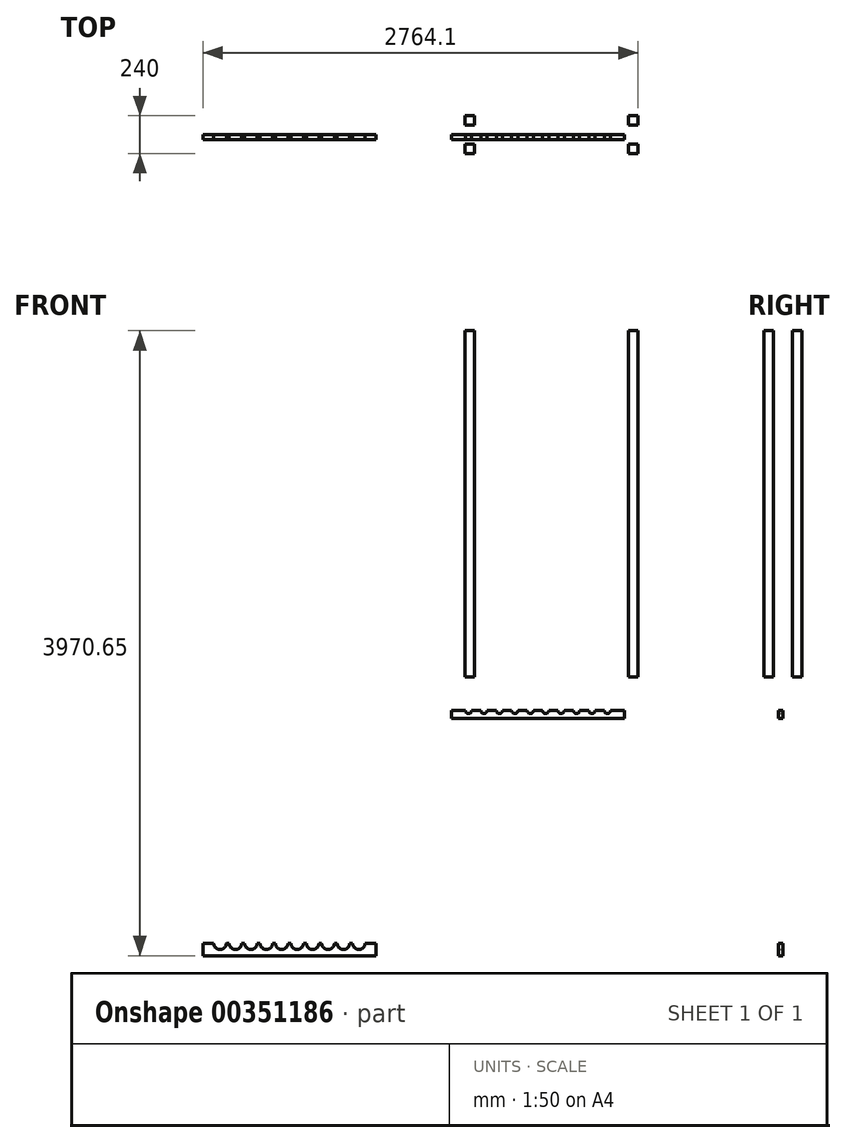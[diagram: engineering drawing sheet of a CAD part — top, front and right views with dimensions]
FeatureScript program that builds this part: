
annotation { "Feature Type Name" : "Feature", "Feature Type Description" : "" }
export const myFeature = defineFeature(function(context is Context, id is Id, definition is map)
    precondition{}
    {
        {
            var Q0;
            Q0=qCreatedBy(makeId("Top.planeOp"),FACE);
            var sketch = newSketch(context, id + "F0", { "sketchPlane" : qUnion([Q0])});
            skLineSegment(sketch, "E0.bottom", {"start": v(-550, -60) * mm, "end": v(-490, -60) * mm});
            skLineSegment(sketch, "E0.top", {"start": v(-550, -120) * mm, "end": v(-490, -120) * mm});
            skLineSegment(sketch, "E0.left", {"start": v(-550, -60) * mm, "end": v(-550, -120) * mm});
            skLineSegment(sketch, "E0.right", {"start": v(-490, -60) * mm, "end": v(-490, -120) * mm});
            skLineSegment(sketch, "E1.bottom", {"start": v(490, -60) * mm, "end": v(550, -60) * mm});
            skLineSegment(sketch, "E1.top", {"start": v(490, -120) * mm, "end": v(550, -120) * mm});
            skLineSegment(sketch, "E1.left", {"start": v(490, -60) * mm, "end": v(490, -120) * mm});
            skLineSegment(sketch, "E1.right", {"start": v(550, -60) * mm, "end": v(550, -120) * mm});
            skLineSegment(sketch, "E2", {"start": v(0, 0) * mm, "end": v(566.52, 0) * mm});
            skLineSegment(sketch, "E3.MirrorCS", {"start": v(550, 60) * mm, "end": v(550, 120) * mm});
            skLineSegment(sketch, "E4.MirrorCS", {"start": v(-550, 60) * mm, "end": v(-550, 120) * mm});
            skLineSegment(sketch, "E5.MirrorCS", {"start": v(-490, 60) * mm, "end": v(-490, 120) * mm});
            skLineSegment(sketch, "E6.MirrorCS", {"start": v(490, 60) * mm, "end": v(490, 120) * mm});
            skLineSegment(sketch, "E7.MirrorCS", {"start": v(490, 60) * mm, "end": v(550, 60) * mm});
            skLineSegment(sketch, "E8.MirrorCS", {"start": v(-550, 120) * mm, "end": v(-490, 120) * mm});
            skLineSegment(sketch, "E9.MirrorCS", {"start": v(-550, 60) * mm, "end": v(-490, 60) * mm});
            skLineSegment(sketch, "E10.MirrorCS", {"start": v(490, 120) * mm, "end": v(550, 120) * mm});
            skSolve(sketch);
        }
        {
            var Q0;
            Q0 = qSketchRegion(id + "F0", true);
            var Q1;
            Q1 = qSketchRegion(id + "FOOtY1L82Ux6p5i_4", true);
            extrude(context, id + "F1", {"entities" : qUnion([Q0, Q1]), "depth" : 2200 * mm});
        }
        {
            var Q0;
            Q0=qCreatedBy(makeId("Front.planeOp"),FACE);
            var sketch = newSketch(context, id + "F2", { "sketchPlane" : qUnion([Q0])});
            skLineSegment(sketch, "E11.bottom", {"start": v(-635.8, -212.51) * mm, "end": v(464.2, -212.51) * mm});
            skLineSegment(sketch, "E11.top", {"start": v(-635.8, -262.51) * mm, "end": v(464.2, -262.51) * mm});
            skLineSegment(sketch, "E11.left", {"start": v(-635.8, -212.51) * mm, "end": v(-635.8, -262.51) * mm});
            skLineSegment(sketch, "E11.right", {"start": v(464.2, -212.51) * mm, "end": v(464.2, -262.51) * mm});
            skCircle(sketch, "E12", {"center": v(-526.8, -212.51) * mm, "radius": 20 * mm});
            skCircle(sketch, "E13.1.0.0", {"center": v(-428.8, -212.51) * mm, "radius": 20 * mm});
            skCircle(sketch, "E13.2.0.0", {"center": v(-330.8, -212.51) * mm, "radius": 20 * mm});
            skCircle(sketch, "E13.3.0.0", {"center": v(-232.8, -212.51) * mm, "radius": 20 * mm});
            skCircle(sketch, "E13.4.0.0", {"center": v(-134.8, -212.51) * mm, "radius": 20 * mm});
            skCircle(sketch, "E13.5.0.0", {"center": v(-36.8, -212.51) * mm, "radius": 20 * mm});
            skCircle(sketch, "E13.6.0.0", {"center": v(61.2, -212.51) * mm, "radius": 20 * mm});
            skCircle(sketch, "E13.7.0.0", {"center": v(159.2, -212.51) * mm, "radius": 20 * mm});
            skCircle(sketch, "E13.8.0.0", {"center": v(257.2, -212.51) * mm, "radius": 20 * mm});
            skCircle(sketch, "E13.9.0.0", {"center": v(355.2, -212.51) * mm, "radius": 20 * mm});
            skLineSegment(sketch, "E13.direction1", {"start": v(-526.8, -212.51) * mm, "end": v(-428.8, -212.51) * mm, "construction": true});
            skLineSegment(sketch, "E14.bottom", {"start": v(-2214.1, -1690.65) * mm, "end": v(-1114.1, -1690.65) * mm});
            skLineSegment(sketch, "E14.top", {"start": v(-2214.1, -1770.65) * mm, "end": v(-1114.1, -1770.65) * mm});
            skLineSegment(sketch, "E14.left", {"start": v(-2214.1, -1690.65) * mm, "end": v(-2214.1, -1770.65) * mm});
            skLineSegment(sketch, "E14.right", {"start": v(-1114.1, -1690.65) * mm, "end": v(-1114.1, -1770.65) * mm});
            skCircle(sketch, "E15", {"center": v(-2105.1, -1690.65) * mm, "radius": 40 * mm});
            skCircle(sketch, "E16.1.0.0", {"center": v(-2007.1, -1690.65) * mm, "radius": 40 * mm});
            skCircle(sketch, "E16.2.0.0", {"center": v(-1909.1, -1690.65) * mm, "radius": 40 * mm});
            skLineSegment(sketch, "E16.direction1", {"start": v(-2105.1, -1690.65) * mm, "end": v(-2007.1, -1690.65) * mm, "construction": true});
            skCircle(sketch, "E17.0.3.0", {"center": v(-1811.1, -1690.65) * mm, "radius": 40 * mm});
            skCircle(sketch, "E17.0.4.0", {"center": v(-1713.1, -1690.65) * mm, "radius": 40 * mm});
            skCircle(sketch, "E17.0.5.0", {"center": v(-1615.1, -1690.65) * mm, "radius": 40 * mm});
            skCircle(sketch, "E17.0.6.0", {"center": v(-1517.1, -1690.65) * mm, "radius": 40 * mm});
            skCircle(sketch, "E17.0.7.0", {"center": v(-1419.1, -1690.65) * mm, "radius": 40 * mm});
            skCircle(sketch, "E17.0.8.0", {"center": v(-1321.1, -1690.65) * mm, "radius": 40 * mm});
            skCircle(sketch, "E17.0.9.0", {"center": v(-1223.1, -1690.65) * mm, "radius": 40 * mm});
            skSolve(sketch);
        }
        {
            var Q0;
            Q0=makeQuery(id+"F2.imprint","IMPRINT",FACE,{"disambiguationData":[TD([[makeQuery(id+"F2.imprint","IMPRINT",EDGE,{"derivedFrom":sQuery(id+"F2.wireOp",EDGE,"E11.top")}),1.0]])]});
            var Q1;
            Q1=makeQuery(id+"F2.imprint","IMPRINT",FACE,{"disambiguationData":[TD([[makeQuery(id+"F2.imprint","IMPRINT",EDGE,{"derivedFrom":sQuery(id+"F2.wireOp",EDGE,"E14.top")}),1.0]])]});
            extrude(context, id + "F3", {"entities" : qUnion([Q0, Q1]), "depth" : 30 * mm});
        }
    });
